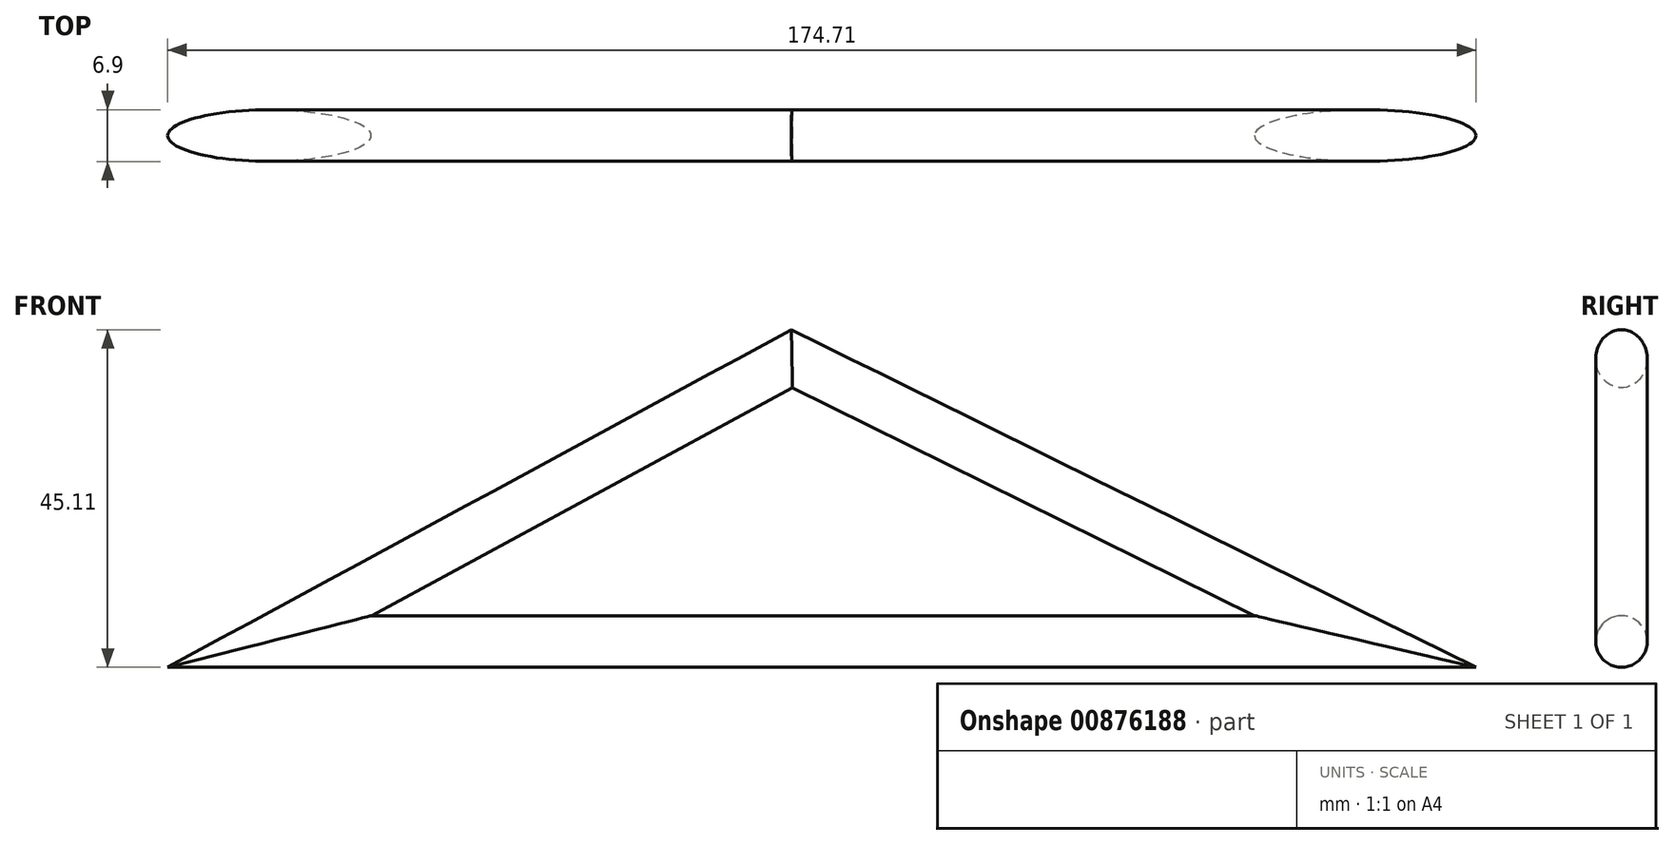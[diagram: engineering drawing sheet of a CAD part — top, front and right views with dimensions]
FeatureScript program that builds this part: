
annotation { "Feature Type Name" : "Feature", "Feature Type Description" : "" }
export const myFeature = defineFeature(function(context is Context, id is Id, definition is map)
    precondition{}
    {
        {
            var Q0;
            Q0=qCreatedBy(makeId("Front.planeOp"),FACE);
            var sketch = newSketch(context, id + "F0", { "sketchPlane" : qUnion([Q0])});
            skLineSegment(sketch, "E0", {"start": v(-69.76, 0) * mm, "end": v(76.56, 0) * mm});
            skLineSegment(sketch, "E1", {"start": v(76.56, 0) * mm, "end": v(0, 37.78) * mm});
            skLineSegment(sketch, "E2", {"start": v(0, 37.78) * mm, "end": v(-69.76, 0) * mm});
            skSolve(sketch);
        }
        {
            var Q0;
            Q0=qCreatedBy(makeId("Right.planeOp"),FACE);
            var sketch = newSketch(context, id + "F1", { "sketchPlane" : qUnion([Q0])});
            skCircle(sketch, "E3", {"center": v(0, 0) * mm, "radius": 3.45 * mm});
            skSolve(sketch);
        }
        {
            var Q0;
            Q0=makeQuery(id+"F1.imprint","IMPRINT",FACE,{"disambiguationData":[TD([[makeQuery(id+"F1.imprint","IMPRINT",EDGE,{"derivedFrom":sQuery(id+"F1.wireOp",EDGE,"E3")}),1.0]])]});
            var Q1;
            Q1=sQuery(id+"F0.wireOp",EDGE,"E0");
            var Q2;
            Q2=sQuery(id+"F0.wireOp",EDGE,"E1");
            var Q3;
            Q3=sQuery(id+"F0.wireOp",EDGE,"E2");
            sweep(context, id + "F2", {"profiles" : qUnion([Q0]), "path" : qUnion([Q1, Q2, Q3])});
        }
    });
